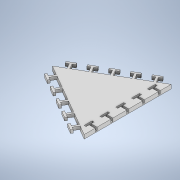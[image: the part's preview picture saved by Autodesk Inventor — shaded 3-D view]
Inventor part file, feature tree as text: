
AUTODESK INVENTOR PART (.ipt)
format: ipt  version: 2022.3 (Build 263350000, 350)  size: 352,256 bytes
history: native  units: mm
features: extrude x5, sketch x3, projected_geometry x1
ambient origin geometry x8: Origin, YZ Plane, XZ Plane, XY Plane, X Axis, Y Axis, Z Axis, Center Point
bodies: Solid1 (feature_tree)
feature tree (9):
  sketch  "Sketch1"  dims[d1=220.0mm d2=35.0mm]
  extrude  "Extrusion1"  Depth=35.0mm
  extrude  "Extrusion2"  Depth=5.0mm
  extrude  "Extrusion3"  Depth=40.0mm
  extrude  "Extrusion4"  Depth=10.0mm TaperAngle=0.0deg
  extrude  "Extrusion5"  Depth=10.0mm TaperAngle=0.0deg
  sketch  "Sketch2"  dims[d3=5.0mm d4=5.0mm]
  projected_geometry  "Projected Loop1"
  sketch  "Sketch3"  dims[d5=20.0mm d6=30.0mm d8=40.0mm d9=30.0mm d11=40.0mm d14=10.0mm d15=0.0mm d16=10.0mm d17=0.0mm d18=2.5mm d19=0.0mm d20=22.0mm d21=5.0mm d22=3.0mm d23=0.0mm d24=15.0mm d25=120.0deg d26=10.0mm d27=5.0mm d28=20.0mm d29=90.0deg d30=5.0mm d31=2.5mm d32=5.0mm d33=20.0mm d35=120.0deg d37=30.0mm d39=40.0mm d40=30.0mm d42=40.0mm d45=30.0mm d47=40.0mm d48=30.0mm d50=40.0mm d53=7.5mm d54=0.0mm]
